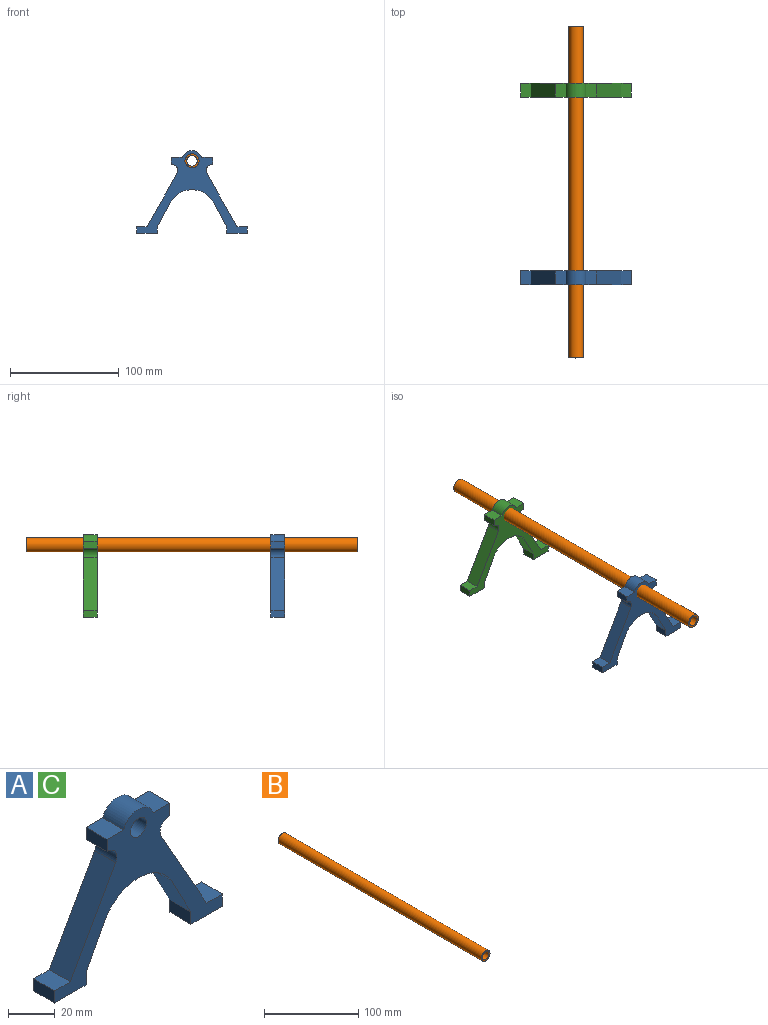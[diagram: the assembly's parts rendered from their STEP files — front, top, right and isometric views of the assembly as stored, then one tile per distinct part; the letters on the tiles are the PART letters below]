
ASSEMBLY  parts=3 mates=2
PART A: 25 faces, bbox 101.6x12.7x76.2 mm
  f0: plane 12.7x6.35mm, normal (-1,0,0), area 80.6mm2, adj f1,f20,f21,f24
  f1: plane 12.7x0.31mm, normal (0,0,-1), area 3.9mm2, adj f0,f2,f20,f21
  f2: cylinder r=5.7mm len=12.7mm, axis (0,1,0), area 150.9mm2, adj f1,f3,f20,f21
  f3: plane 48.65x27.49mm, normal (-0.87,0,0.49), area 709.7mm2, adj f2,f4,f20,f21
  f4: plane 12.7x9.53mm, normal (0,0,1), area 121mm2, adj f3,f5,f20,f21
  f5: plane 12.7x6.35mm, normal (-1,0,0), area 80.6mm2, adj f4,f6,f20,f21
  f6: plane 19.05x12.7mm, normal (0,0,-1), area 241.9mm2, adj f5,f7,f20,f21
  f7: plane 12.7x6.35mm, normal (1,0,0), area 80.6mm2, adj f6,f8,f20,f21
  f8: plane 22.48x12.7mm, normal (0.88,0,-0.47), area 322.6mm2, adj f7,f9,f20,f21
  f9: cylinder r=23.14mm len=39.84mm, axis (0,1,0), area 609.5mm2, adj f8,f10,f20,f21
  f10: plane 22.48x12.7mm, normal (-0.88,0,-0.47), area 322.6mm2, adj f9,f11,f20,f21
  f11: plane 12.7x6.35mm, normal (-1,0,0), area 80.6mm2, adj f10,f12,f20,f21
  f12: plane 19.05x12.7mm, normal (0,0,-1), area 241.9mm2, adj f11,f13,f20,f21
  f13: plane 12.7x6.35mm, normal (1,0,0), area 80.6mm2, adj f12,f14,f20,f21
  f14: plane 12.7x9.53mm, normal (0,0,1), area 121mm2, adj f13,f15,f20,f21
  f15: plane 48.65x27.49mm, normal (0.87,0,0.49), area 709.7mm2, adj f14,f16,f20,f21
  f16: cylinder r=5.7mm len=12.7mm, axis (0,1,0), area 150.9mm2, adj f15,f17,f20,f21
  f17: plane 12.7x0.31mm, normal (0,0,-1), area 3.9mm2, adj f16,f18,f20,f21
  f18: plane 12.7x6.35mm, normal (1,0,0), area 80.6mm2, adj f17,f20,f21,f22
  f19: cylinder r=4.76mm len=12.7mm, axis (0,1,0), area 380mm2, adj f20,f21
  f20: plane 101.6x76.2mm, normal (0,-1,0), area 1929.3mm2, adj f0,f1,f2,f3,f4,f5,f6,f7
  f21: plane 101.6x76.2mm, normal (0,1,0), area 1929.3mm2, adj f0,f1,f2,f3,f4,f5,f6,f7
  f22: plane 12.7x10.07mm, normal (0,0,1), area 127.9mm2, adj f18,f20,f21,f23
  f23: cylinder r=9.53mm len=17.96mm, axis (0,1,0), area 297.8mm2, adj f20,f21,f22,f24
  f24: plane 12.7x10.07mm, normal (0,0,1), area 127.9mm2, adj f0,f20,f21,f23
PART B: 4 faces, bbox 13x304.8x13 mm
  f0: cylinder r=4.76mm len=304.8mm, axis (0,1,0), area 9120.7mm2, adj f2,f3
  f1: cylinder r=6.48mm len=304.8mm, axis (0,1,0), area 12404.2mm2, adj f2,f3
  f2: plane 12.95x12.95mm, normal (0,-1,0), area 60.5mm2, adj f0,f1
  f3: plane 12.95x12.95mm, normal (0,1,0), area 60.5mm2, adj f0,f1
PART C: same geometry as A
PLACE A t=(-16.72,-165.53,-82.8)mm
PLACE B t=(-16.72,59.24,-16.13)mm
PLACE C t=(-16.72,6.62,-82.8)mm
MATE slider B.f0 <-> A.f19  axis (0,1,0) through (-16.72,-93.16,-16.13)mm
MATE slider B.f0 <-> C.f19  axis (0,1,0) through (-16.72,-93.16,-16.13)mm
